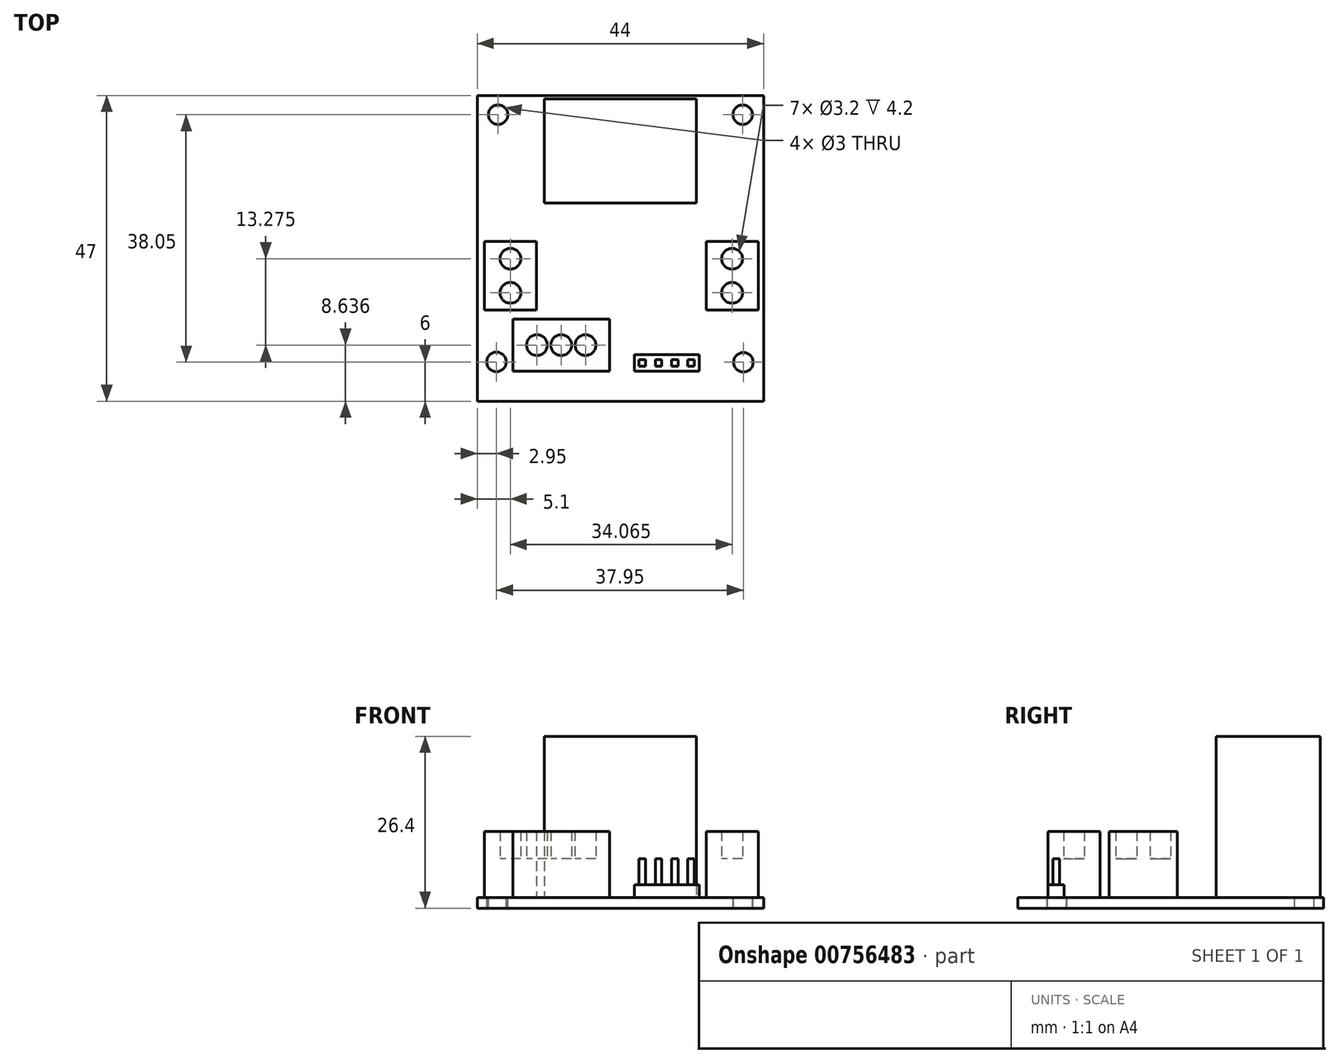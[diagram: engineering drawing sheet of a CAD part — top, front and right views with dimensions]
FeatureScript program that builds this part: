
annotation { "Feature Type Name" : "Feature", "Feature Type Description" : "" }
export const myFeature = defineFeature(function(context is Context, id is Id, definition is map)
    precondition{}
    {
        {
            var Q0;
            Q0=qCreatedBy(makeId("Top.planeOp"),FACE);
            var sketch = newSketch(context, id + "F0", { "sketchPlane" : qUnion([Q0])});
            skLineSegment(sketch, "E0.bottom", {"start": v(-22, -23.5) * mm, "end": v(22, -23.5) * mm});
            skLineSegment(sketch, "E0.top", {"start": v(-22, 23.5) * mm, "end": v(22, 23.5) * mm});
            skLineSegment(sketch, "E0.left", {"start": v(-22, -23.5) * mm, "end": v(-22, 23.5) * mm});
            skLineSegment(sketch, "E0.right", {"start": v(22, -23.5) * mm, "end": v(22, 23.5) * mm});
            skPoint(sketch, "E0.middle", {"position": v(0, 0) * mm});
            skCircle(sketch, "E1", {"center": v(18.8, 20.55) * mm, "radius": 1.5 * mm});
            skCircle(sketch, "E2", {"center": v(-18.8, 20.55) * mm, "radius": 1.5 * mm});
            skCircle(sketch, "E3", {"center": v(-19.05, -17.45) * mm, "radius": 1.5 * mm});
            skCircle(sketch, "E4", {"center": v(18.9, -17.5) * mm, "radius": 1.5 * mm});
            skLineSegment(sketch, "E5.bottom", {"start": v(-11.7, 7) * mm, "end": v(11.7, 7) * mm});
            skLineSegment(sketch, "E5.top", {"start": v(-11.7, 23) * mm, "end": v(11.7, 23) * mm});
            skLineSegment(sketch, "E5.left", {"start": v(-11.7, 7) * mm, "end": v(-11.7, 23) * mm});
            skLineSegment(sketch, "E5.right", {"start": v(11.7, 7) * mm, "end": v(11.7, 23) * mm});
            skPoint(sketch, "E5.middle", {"position": v(0, 15) * mm});
            skLineSegment(sketch, "E6.bottom", {"start": v(21.16, -9.46) * mm, "end": v(13.16, -9.46) * mm});
            skLineSegment(sketch, "E6.top", {"start": v(21.16, 1.04) * mm, "end": v(13.16, 1.04) * mm});
            skLineSegment(sketch, "E6.left", {"start": v(21.16, -9.46) * mm, "end": v(21.16, 1.04) * mm});
            skLineSegment(sketch, "E6.right", {"start": v(13.16, -9.46) * mm, "end": v(13.16, 1.04) * mm});
            skPoint(sketch, "E6.middle", {"position": v(17.16, -4.21) * mm});
            skLineSegment(sketch, "E7.bottom", {"start": v(-12.9, -9.46) * mm, "end": v(-20.9, -9.46) * mm});
            skLineSegment(sketch, "E7.top", {"start": v(-12.9, 1.04) * mm, "end": v(-20.9, 1.04) * mm});
            skLineSegment(sketch, "E7.left", {"start": v(-12.9, -9.46) * mm, "end": v(-12.9, 1.04) * mm});
            skLineSegment(sketch, "E7.right", {"start": v(-20.9, -9.46) * mm, "end": v(-20.9, 1.04) * mm});
            skPoint(sketch, "E7.middle", {"position": v(-16.9, -4.21) * mm});
            skLineSegment(sketch, "E8.bottom", {"start": v(-16.55, -18.86) * mm, "end": v(-1.65, -18.86) * mm});
            skLineSegment(sketch, "E8.top", {"start": v(-16.55, -10.86) * mm, "end": v(-1.65, -10.86) * mm});
            skLineSegment(sketch, "E8.left", {"start": v(-16.55, -18.86) * mm, "end": v(-16.55, -10.86) * mm});
            skLineSegment(sketch, "E8.right", {"start": v(-1.65, -18.86) * mm, "end": v(-1.65, -10.86) * mm});
            skLineSegment(sketch, "E9", {"start": v(-16.9, 1.04) * mm, "end": v(-16.9, -4.21) * mm, "construction": true});
            skLineSegment(sketch, "E10", {"start": v(-16.9, -4.21) * mm, "end": v(-16.9, -9.46) * mm, "construction": true});
            skPoint(sketch, "E11", {"position": v(-16.9, -1.59) * mm});
            skPoint(sketch, "E12", {"position": v(-16.9, -6.84) * mm});
            skLineSegment(sketch, "E13", {"start": v(17.16, -4.21) * mm, "end": v(17.16, 1.04) * mm, "construction": true});
            skLineSegment(sketch, "E14", {"start": v(17.16, -4.21) * mm, "end": v(17.16, -9.46) * mm, "construction": true});
            skPoint(sketch, "E15", {"position": v(17.16, -1.59) * mm});
            skPoint(sketch, "E16", {"position": v(17.16, -6.84) * mm});
            skCircle(sketch, "E17", {"center": v(-16.9, -1.59) * mm, "radius": 1.6 * mm});
            skCircle(sketch, "E18", {"center": v(-16.9, -6.84) * mm, "radius": 1.6 * mm});
            skCircle(sketch, "E19", {"center": v(17.16, -1.59) * mm, "radius": 1.6 * mm});
            skCircle(sketch, "E20", {"center": v(17.16, -6.84) * mm, "radius": 1.6 * mm});
            skPoint(sketch, "E21", {"position": v(-9.1, -14.86) * mm});
            skLineSegment(sketch, "E22", {"start": v(-9.1, -14.86) * mm, "end": v(-1.65, -14.86) * mm, "construction": true});
            skLineSegment(sketch, "E23", {"start": v(-9.1, -14.86) * mm, "end": v(-16.55, -14.86) * mm, "construction": true});
            skPoint(sketch, "E24", {"position": v(-12.82, -14.86) * mm});
            skPoint(sketch, "E25", {"position": v(-5.37, -14.86) * mm});
            skCircle(sketch, "E26", {"center": v(-12.82, -14.86) * mm, "radius": 1.6 * mm});
            skCircle(sketch, "E27", {"center": v(-9.1, -14.86) * mm, "radius": 1.6 * mm});
            skCircle(sketch, "E28", {"center": v(-5.37, -14.86) * mm, "radius": 1.6 * mm});
            skLineSegment(sketch, "E29.left", {"start": v(2.12, -18.86) * mm, "end": v(2.12, -16.36) * mm});
            skLineSegment(sketch, "E29.right", {"start": v(12.12, -18.86) * mm, "end": v(12.12, -16.36) * mm});
            skPoint(sketch, "E30", {"position": v(7.12, -16.36) * mm});
            skLineSegment(sketch, "E31", {"start": v(2.12, -18.86) * mm, "end": v(12.12, -18.86) * mm});
            skPoint(sketch, "E32", {"position": v(4.62, -16.36) * mm});
            skPoint(sketch, "E33", {"position": v(9.62, -16.36) * mm});
            skLineSegment(sketch, "E34", {"start": v(4.62, -16.36) * mm, "end": v(4.62, -18.86) * mm});
            skLineSegment(sketch, "E35", {"start": v(9.62, -16.36) * mm, "end": v(9.62, -18.86) * mm});
            skLineSegment(sketch, "E36", {"start": v(2.12, -16.36) * mm, "end": v(4.62, -16.36) * mm});
            skLineSegment(sketch, "E37", {"start": v(4.62, -16.36) * mm, "end": v(7.12, -16.36) * mm});
            skLineSegment(sketch, "E38", {"start": v(7.12, -16.36) * mm, "end": v(9.62, -16.36) * mm});
            skLineSegment(sketch, "E39", {"start": v(9.62, -16.36) * mm, "end": v(12.12, -16.36) * mm});
            skPoint(sketch, "E40", {"position": v(3.37, -17.61) * mm});
            skPoint(sketch, "E40.positionSnap0", {"position": v(4.62, -17.61) * mm});
            skPoint(sketch, "E40.positionSnap1", {"position": v(3.37, -16.36) * mm});
            skPoint(sketch, "E41", {"position": v(5.87, -17.61) * mm});
            skPoint(sketch, "E41.positionSnap0", {"position": v(5.87, -16.36) * mm});
            skPoint(sketch, "E42", {"position": v(8.37, -17.61) * mm});
            skPoint(sketch, "E42.positionSnap1", {"position": v(8.37, -16.36) * mm});
            skPoint(sketch, "E43", {"position": v(10.87, -17.61) * mm});
            skPoint(sketch, "E43.positionSnap0", {"position": v(10.87, -16.36) * mm});
            skPoint(sketch, "E43.positionSnap1", {"position": v(9.62, -17.61) * mm});
            skLineSegment(sketch, "E44.bottom", {"start": v(2.87, -18.11) * mm, "end": v(3.87, -18.11) * mm});
            skLineSegment(sketch, "E44.top", {"start": v(2.87, -17.11) * mm, "end": v(3.87, -17.11) * mm});
            skLineSegment(sketch, "E44.left", {"start": v(2.87, -18.11) * mm, "end": v(2.87, -17.11) * mm});
            skLineSegment(sketch, "E44.right", {"start": v(3.87, -18.11) * mm, "end": v(3.87, -17.11) * mm});
            skLineSegment(sketch, "E45.bottom", {"start": v(5.37, -18.11) * mm, "end": v(6.37, -18.11) * mm});
            skLineSegment(sketch, "E45.top", {"start": v(5.37, -17.11) * mm, "end": v(6.37, -17.11) * mm});
            skLineSegment(sketch, "E45.left", {"start": v(5.37, -18.11) * mm, "end": v(5.37, -17.11) * mm});
            skLineSegment(sketch, "E45.right", {"start": v(6.37, -18.11) * mm, "end": v(6.37, -17.11) * mm});
            skLineSegment(sketch, "E46", {"start": v(7.12, -16.36) * mm, "end": v(7.12, -18.86) * mm});
            skLineSegment(sketch, "E47.bottom", {"start": v(7.87, -18.11) * mm, "end": v(8.87, -18.11) * mm});
            skLineSegment(sketch, "E47.top", {"start": v(7.87, -17.11) * mm, "end": v(8.87, -17.11) * mm});
            skLineSegment(sketch, "E47.left", {"start": v(7.87, -18.11) * mm, "end": v(7.87, -17.11) * mm});
            skLineSegment(sketch, "E47.right", {"start": v(8.87, -18.11) * mm, "end": v(8.87, -17.11) * mm});
            skLineSegment(sketch, "E48.bottom", {"start": v(10.37, -18.11) * mm, "end": v(11.37, -18.11) * mm});
            skLineSegment(sketch, "E48.top", {"start": v(10.37, -17.11) * mm, "end": v(11.37, -17.11) * mm});
            skLineSegment(sketch, "E48.left", {"start": v(10.37, -18.11) * mm, "end": v(10.37, -17.11) * mm});
            skLineSegment(sketch, "E48.right", {"start": v(11.37, -18.11) * mm, "end": v(11.37, -17.11) * mm});
            skSolve(sketch);
        }
        {
            var Q0;
            Q0=makeQuery(id+"F0.imprint","IMPRINT",FACE,{"disambiguationData":[TD([[makeQuery(id+"F0.imprint","IMPRINT",EDGE,{"derivedFrom":sQuery(id+"F0.wireOp",EDGE,"E0.bottom")}),1.0]])]});
            var Q1;
            Q1=makeQuery(id+"F0.imprint","IMPRINT",FACE,{"disambiguationData":[TD([[makeQuery(id+"F0.imprint","IMPRINT",EDGE,{"derivedFrom":sQuery(id+"F0.wireOp",EDGE,"E5.bottom")}),1.0]])]});
            var Q2;
            Q2=makeQuery(id+"F0.imprint","IMPRINT",FACE,{"disambiguationData":[TD([[makeQuery(id+"F0.imprint","IMPRINT",EDGE,{"derivedFrom":sQuery(id+"F0.wireOp",EDGE,"E6.bottom")}),-1.0]])]});
            var Q3;
            Q3=makeQuery(id+"F0.imprint","IMPRINT",FACE,{"disambiguationData":[TD([[makeQuery(id+"F0.imprint","IMPRINT",EDGE,{"derivedFrom":sQuery(id+"F0.wireOp",EDGE,"E8.bottom")}),1.0]])]});
            var Q4;
            Q4=makeQuery(id+"F0.imprint","IMPRINT",FACE,{"disambiguationData":[TD([[makeQuery(id+"F0.imprint","IMPRINT",EDGE,{"derivedFrom":sQuery(id+"F0.wireOp",EDGE,"E7.bottom")}),-1.0]])]});
            var Q5;
            Q5=makeQuery(id+"F0.imprint","IMPRINT",FACE,{"disambiguationData":[TD([[makeQuery(id+"F0.imprint","IMPRINT",EDGE,{"derivedFrom":sQuery(id+"F0.wireOp",EDGE,"E17")}),1.0]])]});
            var Q6;
            Q6=makeQuery(id+"F0.imprint","IMPRINT",FACE,{"disambiguationData":[TD([[makeQuery(id+"F0.imprint","IMPRINT",EDGE,{"derivedFrom":sQuery(id+"F0.wireOp",EDGE,"E18")}),1.0]])]});
            var Q7;
            Q7=makeQuery(id+"F0.imprint","IMPRINT",FACE,{"disambiguationData":[TD([[makeQuery(id+"F0.imprint","IMPRINT",EDGE,{"derivedFrom":sQuery(id+"F0.wireOp",EDGE,"E26")}),1.0]])]});
            var Q8;
            Q8=makeQuery(id+"F0.imprint","IMPRINT",FACE,{"disambiguationData":[TD([[makeQuery(id+"F0.imprint","IMPRINT",EDGE,{"derivedFrom":sQuery(id+"F0.wireOp",EDGE,"E27")}),1.0]])]});
            var Q9;
            Q9=makeQuery(id+"F0.imprint","IMPRINT",FACE,{"disambiguationData":[TD([[makeQuery(id+"F0.imprint","IMPRINT",EDGE,{"derivedFrom":sQuery(id+"F0.wireOp",EDGE,"E28")}),1.0]])]});
            var Q10;
            Q10=makeQuery(id+"F0.imprint","IMPRINT",FACE,{"disambiguationData":[TD([[makeQuery(id+"F0.imprint","IMPRINT",EDGE,{"derivedFrom":sQuery(id+"F0.wireOp",EDGE,"E20")}),1.0]])]});
            var Q11;
            Q11=makeQuery(id+"F0.imprint","IMPRINT",FACE,{"disambiguationData":[TD([[makeQuery(id+"F0.imprint","IMPRINT",EDGE,{"derivedFrom":sQuery(id+"F0.wireOp",EDGE,"E19")}),1.0]])]});
            var Q12;
            {var subQ2=sQuery(id+"F0.wireOp",EDGE,"E29.left");Q12=makeQuery(id+"F0.imprint","IMPRINT",FACE,{"disambiguationData":[TD([[makeQuery(id+"F0.imprint","IMPRINT",EDGE,{"derivedFrom":subQ2}),-1.0]])]});}
            var Q13;
            Q13=makeQuery(id+"F0.imprint","IMPRINT",FACE,{"disambiguationData":[TD([[makeQuery(id+"F0.imprint","IMPRINT",EDGE,{"derivedFrom":sQuery(id+"F0.wireOp",EDGE,"E44.bottom")}),1.0]])]});
            var Q14;
            {var subQ1=sQuery(id+"F0.wireOp",EDGE,"E34");Q14=makeQuery(id+"F0.imprint","IMPRINT",FACE,{"disambiguationData":[TD([[makeQuery(id+"F0.imprint","IMPRINT",EDGE,{"derivedFrom":subQ1}),1.0]])]});}
            var Q15;
            Q15=makeQuery(id+"F0.imprint","IMPRINT",FACE,{"disambiguationData":[TD([[makeQuery(id+"F0.imprint","IMPRINT",EDGE,{"derivedFrom":sQuery(id+"F0.wireOp",EDGE,"E45.bottom")}),1.0]])]});
            var Q16;
            {var subQ1=sQuery(id+"F0.wireOp",EDGE,"E35");Q16=makeQuery(id+"F0.imprint","IMPRINT",FACE,{"disambiguationData":[TD([[makeQuery(id+"F0.imprint","IMPRINT",EDGE,{"derivedFrom":subQ1}),-1.0]])]});}
            var Q17;
            Q17=makeQuery(id+"F0.imprint","IMPRINT",FACE,{"disambiguationData":[TD([[makeQuery(id+"F0.imprint","IMPRINT",EDGE,{"derivedFrom":sQuery(id+"F0.wireOp",EDGE,"E48.bottom")}),1.0]])]});
            var Q18;
            {var subQ2=sQuery(id+"F0.wireOp",EDGE,"E29.right");Q18=makeQuery(id+"F0.imprint","IMPRINT",FACE,{"disambiguationData":[TD([[makeQuery(id+"F0.imprint","IMPRINT",EDGE,{"derivedFrom":subQ2}),1.0]])]});}
            var Q19;
            Q19=makeQuery(id+"F0.imprint","IMPRINT",FACE,{"disambiguationData":[TD([[makeQuery(id+"F0.imprint","IMPRINT",EDGE,{"derivedFrom":sQuery(id+"F0.wireOp",EDGE,"E47.bottom")}),1.0]])]});
            extrude(context, id + "F1", {"entities" : qUnion([Q0, Q1, Q2, Q3, Q4, Q5, Q6, Q7, Q8, Q9, Q10, Q11, Q12, Q13, Q14, Q15, Q16, Q17, Q18, Q19]), "oppositeDirection" : true, "depth" : 1.6 * mm, "offsetDistance" : 25 * mm});
        }
        {
            var Q0;
            Q0=makeQuery(id+"F0.imprint","IMPRINT",FACE,{"disambiguationData":[TD([[makeQuery(id+"F0.imprint","IMPRINT",EDGE,{"derivedFrom":sQuery(id+"F0.wireOp",EDGE,"E5.bottom")}),1.0]])]});
            extrude(context, id + "F2", {"entities" : qUnion([Q0]), "operationType" : NewBodyOperationType.ADD, "depth" : 24.8 * mm, "offsetDistance" : 25 * mm});
        }
        {
            var Q0;
            Q0=makeQuery(id+"F0.imprint","IMPRINT",FACE,{"disambiguationData":[TD([[makeQuery(id+"F0.imprint","IMPRINT",EDGE,{"derivedFrom":sQuery(id+"F0.wireOp",EDGE,"E7.bottom")}),-1.0]])]});
            var Q1;
            Q1=makeQuery(id+"F0.imprint","IMPRINT",FACE,{"disambiguationData":[TD([[makeQuery(id+"F0.imprint","IMPRINT",EDGE,{"derivedFrom":sQuery(id+"F0.wireOp",EDGE,"E8.bottom")}),1.0]])]});
            var Q2;
            Q2=makeQuery(id+"F0.imprint","IMPRINT",FACE,{"disambiguationData":[TD([[makeQuery(id+"F0.imprint","IMPRINT",EDGE,{"derivedFrom":sQuery(id+"F0.wireOp",EDGE,"E6.bottom")}),-1.0]])]});
            extrude(context, id + "F3", {"entities" : qUnion([Q0, Q1, Q2]), "operationType" : NewBodyOperationType.ADD, "depth" : 10.2 * mm, "offsetDistance" : 25 * mm});
        }
        {
            var Q0;
            Q0=makeQuery(id+"F0.imprint","IMPRINT",FACE,{"disambiguationData":[TD([[makeQuery(id+"F0.imprint","IMPRINT",EDGE,{"derivedFrom":sQuery(id+"F0.wireOp",EDGE,"E17")}),1.0]])]});
            var Q1;
            Q1=makeQuery(id+"F0.imprint","IMPRINT",FACE,{"disambiguationData":[TD([[makeQuery(id+"F0.imprint","IMPRINT",EDGE,{"derivedFrom":sQuery(id+"F0.wireOp",EDGE,"E18")}),1.0]])]});
            var Q2;
            Q2=makeQuery(id+"F0.imprint","IMPRINT",FACE,{"disambiguationData":[TD([[makeQuery(id+"F0.imprint","IMPRINT",EDGE,{"derivedFrom":sQuery(id+"F0.wireOp",EDGE,"E26")}),1.0]])]});
            var Q3;
            Q3=makeQuery(id+"F0.imprint","IMPRINT",FACE,{"disambiguationData":[TD([[makeQuery(id+"F0.imprint","IMPRINT",EDGE,{"derivedFrom":sQuery(id+"F0.wireOp",EDGE,"E27")}),1.0]])]});
            var Q4;
            Q4=makeQuery(id+"F0.imprint","IMPRINT",FACE,{"disambiguationData":[TD([[makeQuery(id+"F0.imprint","IMPRINT",EDGE,{"derivedFrom":sQuery(id+"F0.wireOp",EDGE,"E28")}),1.0]])]});
            var Q5;
            Q5=makeQuery(id+"F0.imprint","IMPRINT",FACE,{"disambiguationData":[TD([[makeQuery(id+"F0.imprint","IMPRINT",EDGE,{"derivedFrom":sQuery(id+"F0.wireOp",EDGE,"E20")}),1.0]])]});
            var Q6;
            Q6=makeQuery(id+"F0.imprint","IMPRINT",FACE,{"disambiguationData":[TD([[makeQuery(id+"F0.imprint","IMPRINT",EDGE,{"derivedFrom":sQuery(id+"F0.wireOp",EDGE,"E19")}),1.0]])]});
            extrude(context, id + "F4", {"entities" : qUnion([Q0, Q1, Q2, Q3, Q4, Q5, Q6]), "operationType" : NewBodyOperationType.ADD, "depth" : 6 * mm, "offsetDistance" : 25 * mm});
        }
        {
            var Q0;
            {var subQ2=sQuery(id+"F0.wireOp",EDGE,"E29.left");Q0=makeQuery(id+"F0.imprint","IMPRINT",FACE,{"disambiguationData":[TD([[makeQuery(id+"F0.imprint","IMPRINT",EDGE,{"derivedFrom":subQ2}),-1.0]])]});}
            var Q1;
            {var subQ1=sQuery(id+"F0.wireOp",EDGE,"E34");Q1=makeQuery(id+"F0.imprint","IMPRINT",FACE,{"disambiguationData":[TD([[makeQuery(id+"F0.imprint","IMPRINT",EDGE,{"derivedFrom":subQ1}),1.0]])]});}
            var Q2;
            {var subQ1=sQuery(id+"F0.wireOp",EDGE,"E35");Q2=makeQuery(id+"F0.imprint","IMPRINT",FACE,{"disambiguationData":[TD([[makeQuery(id+"F0.imprint","IMPRINT",EDGE,{"derivedFrom":subQ1}),-1.0]])]});}
            var Q3;
            {var subQ2=sQuery(id+"F0.wireOp",EDGE,"E29.right");Q3=makeQuery(id+"F0.imprint","IMPRINT",FACE,{"disambiguationData":[TD([[makeQuery(id+"F0.imprint","IMPRINT",EDGE,{"derivedFrom":subQ2}),1.0]])]});}
            extrude(context, id + "F5", {"entities" : qUnion([Q0, Q1, Q2, Q3]), "operationType" : NewBodyOperationType.ADD, "depth" : 2 * mm, "offsetDistance" : 25 * mm});
        }
        {
            var Q0;
            Q0=makeQuery(id+"F0.imprint","IMPRINT",FACE,{"disambiguationData":[TD([[makeQuery(id+"F0.imprint","IMPRINT",EDGE,{"derivedFrom":sQuery(id+"F0.wireOp",EDGE,"E44.bottom")}),1.0]])]});
            var Q1;
            Q1=makeQuery(id+"F0.imprint","IMPRINT",FACE,{"disambiguationData":[TD([[makeQuery(id+"F0.imprint","IMPRINT",EDGE,{"derivedFrom":sQuery(id+"F0.wireOp",EDGE,"E45.bottom")}),1.0]])]});
            var Q2;
            Q2=makeQuery(id+"F0.imprint","IMPRINT",FACE,{"disambiguationData":[TD([[makeQuery(id+"F0.imprint","IMPRINT",EDGE,{"derivedFrom":sQuery(id+"F0.wireOp",EDGE,"E47.bottom")}),1.0]])]});
            var Q3;
            Q3=makeQuery(id+"F0.imprint","IMPRINT",FACE,{"disambiguationData":[TD([[makeQuery(id+"F0.imprint","IMPRINT",EDGE,{"derivedFrom":sQuery(id+"F0.wireOp",EDGE,"E48.bottom")}),1.0]])]});
            extrude(context, id + "F6", {"entities" : qUnion([Q0, Q1, Q2, Q3]), "operationType" : NewBodyOperationType.ADD, "depth" : 6 * mm, "offsetDistance" : 25 * mm});
        }
    });
